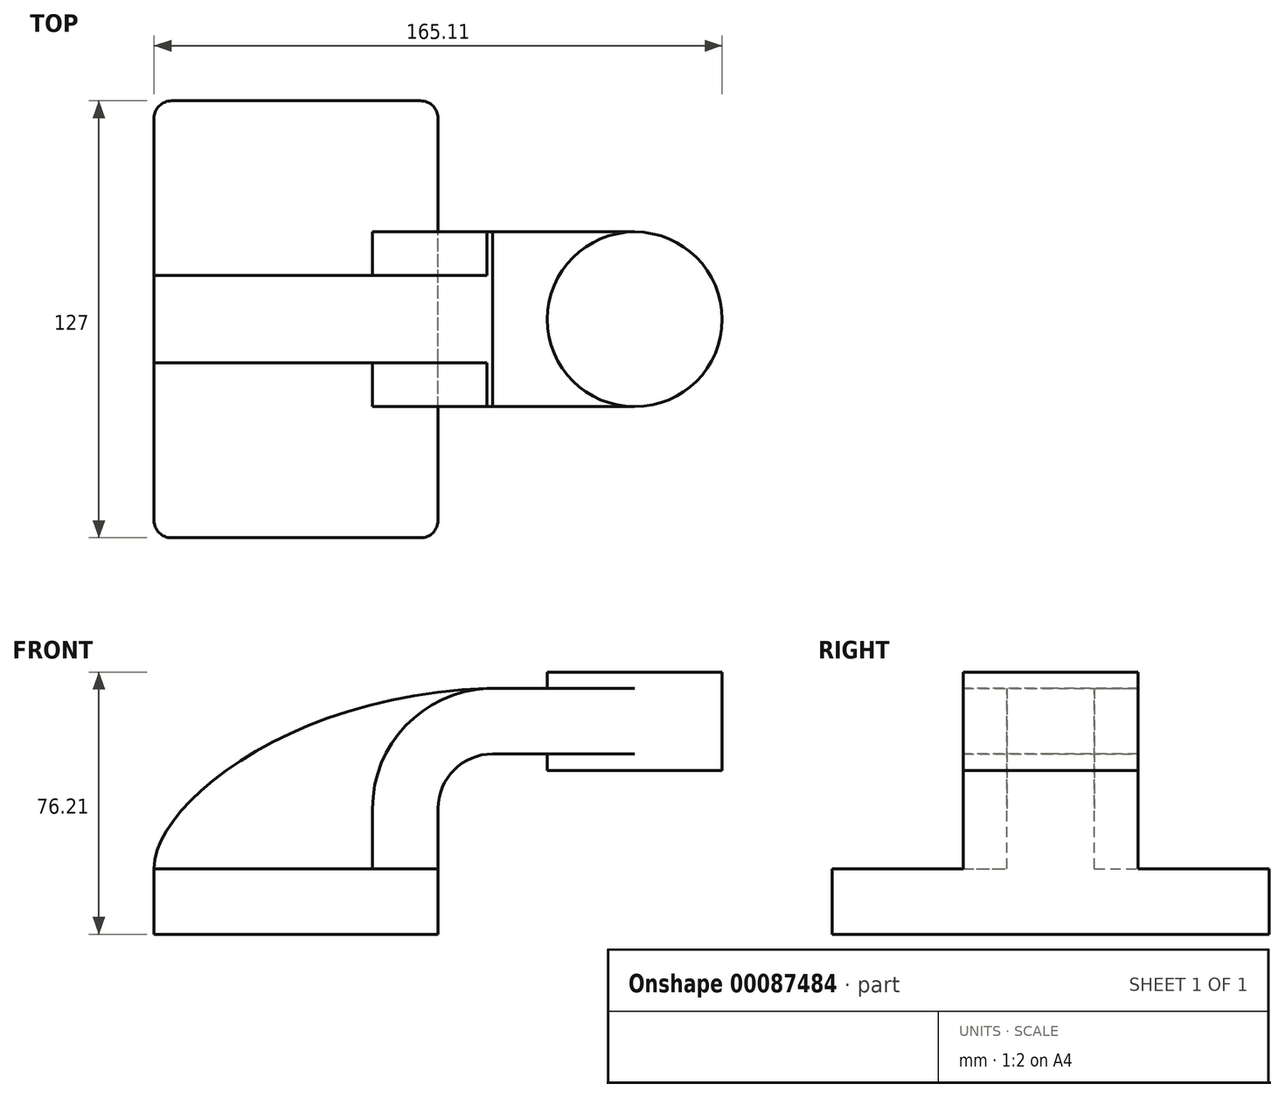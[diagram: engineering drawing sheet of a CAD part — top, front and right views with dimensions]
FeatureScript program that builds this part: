
annotation { "Feature Type Name" : "Feature", "Feature Type Description" : "" }
export const myFeature = defineFeature(function(context is Context, id is Id, definition is map)
    precondition{}
    {
        {
            var Q0;
            Q0=qCreatedBy(makeId("Front.planeOp"),FACE);
            var sketch = newSketch(context, id + "F0", { "sketchPlane" : qUnion([Q0])});
            skLineSegment(sketch, "E0.bottom", {"start": v(41.28, -9.52) * mm, "end": v(-41.28, -9.53) * mm});
            skLineSegment(sketch, "E0.top", {"start": v(41.28, 9.53) * mm, "end": v(-41.28, 9.53) * mm});
            skLineSegment(sketch, "E0.left", {"start": v(41.28, -9.52) * mm, "end": v(41.28, 9.53) * mm});
            skLineSegment(sketch, "E0.right", {"start": v(-41.28, -9.53) * mm, "end": v(-41.28, 9.53) * mm});
            skPoint(sketch, "E0.middle", {"position": v(0, 0) * mm});
            skLineSegment(sketch, "E1.bottom", {"start": v(73.02, 66.68) * mm, "end": v(123.82, 66.68) * mm});
            skLineSegment(sketch, "E1.top", {"start": v(73.02, 38.1) * mm, "end": v(123.82, 38.1) * mm});
            skLineSegment(sketch, "E1.left", {"start": v(73.03, 66.68) * mm, "end": v(73.03, 38.1) * mm});
            skLineSegment(sketch, "E1.right", {"start": v(123.83, 66.68) * mm, "end": v(123.83, 38.1) * mm});
            skPoint(sketch, "E1.middle", {"position": v(98.42, 52.39) * mm});
            skLineSegment(sketch, "E2", {"start": v(41.28, 9.53) * mm, "end": v(41.28, 27) * mm});
            skArc(sketch, "E3", {"start": v(41.27, 27) * mm, "mid": v(45.92, 38.23) * mm, "end": v(57.15, 42.88) * mm});
            skLineSegment(sketch, "E4", {"start": v(57.15, 42.88) * mm, "end": v(98.42, 42.88) * mm});
            skPoint(sketch, "E4.endSnap0", {"position": v(98.42, 38.1) * mm});
            skLineSegment(sketch, "E5.0", {"start": v(57.15, 61.93) * mm, "end": v(98.42, 61.93) * mm});
            skArc(sketch, "E5.1", {"start": v(22.22, 27) * mm, "mid": v(32.45, 51.7) * mm, "end": v(57.15, 61.93) * mm});
            skLineSegment(sketch, "E5.2", {"start": v(22.23, 9.53) * mm, "end": v(22.23, 27) * mm});
            skLineSegment(sketch, "E6", {"start": v(98.42, 38.1) * mm, "end": v(98.42, 66.68) * mm});
            skFitSpline(sketch, "E7", {"points": [v(-41.28, 9.53) * mm, v(57.15, 61.93) * mm], "startDerivative": vector(0.2, 58.25) * mm, "endDerivative": vector(171.45, 3.3) * mm});
            skSolve(sketch);
        }
        {
            var Q0;
            Q0=makeQuery(id+"F0.imprint","IMPRINT",FACE,{"disambiguationData":[TD([[makeQuery(id+"F0.imprint","IMPRINT",EDGE,{"derivedFrom":sQuery(id+"F0.wireOp",EDGE,"E0.bottom")}),-1.0]])]});
            extrude(context, id + "F1", {"entities" : qUnion([Q0]), "endBound" : BoundingType.SYMMETRIC, "depth" : 127 * mm});
        }
        {
            var Q0;
            {var subQ1=sQuery(id+"F0.wireOp",EDGE,"E2");Q0=makeQuery(id+"F0.imprint","IMPRINT",FACE,{"disambiguationData":[TD([[makeQuery(id+"F0.imprint","IMPRINT",EDGE,{"derivedFrom":subQ1}),1.0]])]});}
            var Q1;
            {var subQ0=sQuery(id+"F0.wireOp",EDGE,"E5.0");var subQ1=sQuery(id+"F0.wireOp",EDGE,"E1.left");var subQ2=makeQuery(id+"F0.imprint","INTERSECT",VERTEX,{"derivedFrom":[subQ1,subQ0]});Q1=makeQuery(id+"F0.imprint","IMPRINT",FACE,{"disambiguationData":[TD([[makeQuery(id+"F0.imprint","IMPRINT",EDGE,{"disambiguationData":[TD([[subQ2,-1.0]])],"derivedFrom":subQ1}),1.0]])]});}
            extrude(context, id + "F2", {"entities" : qUnion([Q0, Q1]), "operationType" : NewBodyOperationType.ADD, "endBound" : BoundingType.SYMMETRIC, "depth" : 50.8 * mm});
        }
        {
            var Q0;
            {var subQ3=sQuery(id+"F0.wireOp",EDGE,"E5.2");Q0=makeQuery(id+"F0.imprint","IMPRINT",FACE,{"disambiguationData":[TD([[makeQuery(id+"F0.imprint","IMPRINT",EDGE,{"derivedFrom":subQ3}),1.0]])]});}
            extrude(context, id + "F3", {"entities" : qUnion([Q0]), "operationType" : NewBodyOperationType.ADD, "endBound" : BoundingType.SYMMETRIC, "depth" : 25.4 * mm});
        }
        {
            var Q0;
            {var subQ0=sQuery(id+"F0.wireOp",EDGE,"E1.right");Q0=makeQuery(id+"F0.imprint","IMPRINT",FACE,{"disambiguationData":[TD([[makeQuery(id+"F0.imprint","IMPRINT",EDGE,{"derivedFrom":subQ0}),-1.0]])]});}
            var Q1;
            Q1=sQuery(id+"F0.wireOp",EDGE,"E6");
            revolve(context, id + "F4", {"operationType" : NewBodyOperationType.ADD, "entities" : qUnion([Q0]), "axis" : qUnion([Q1]), "revolveType" : RevolveType.FULL});
        }
        {
            var Q0;
            Q0=makeQuery(id+"F1.opExtrude","CAP_EDGE",EDGE,{"disambiguationData":[OSD([sQuery(id+"F0.wireOp",EDGE,"E0.left")])],"isStart":false});
            var Q1;
            Q1=makeQuery(id+"F1.opExtrude","CAP_EDGE",EDGE,{"disambiguationData":[OSD([sQuery(id+"F0.wireOp",EDGE,"E0.right")])],"isStart":false});
            var Q2;
            Q2=makeQuery(id+"F1.opExtrude","CAP_EDGE",EDGE,{"disambiguationData":[OSD([sQuery(id+"F0.wireOp",EDGE,"E0.right")])],"isStart":true});
            var Q3;
            Q3=makeQuery(id+"F1.opExtrude","CAP_EDGE",EDGE,{"disambiguationData":[OSD([sQuery(id+"F0.wireOp",EDGE,"E0.left")])],"isStart":true});
            fillet(context, id + "F5", {"entities" : qUnion([Q0, Q1, Q2, Q3]), "radius" : 5.08 * mm, "tangentPropagation" : true, "allowEdgeOverflow" : false});
        }
    });
